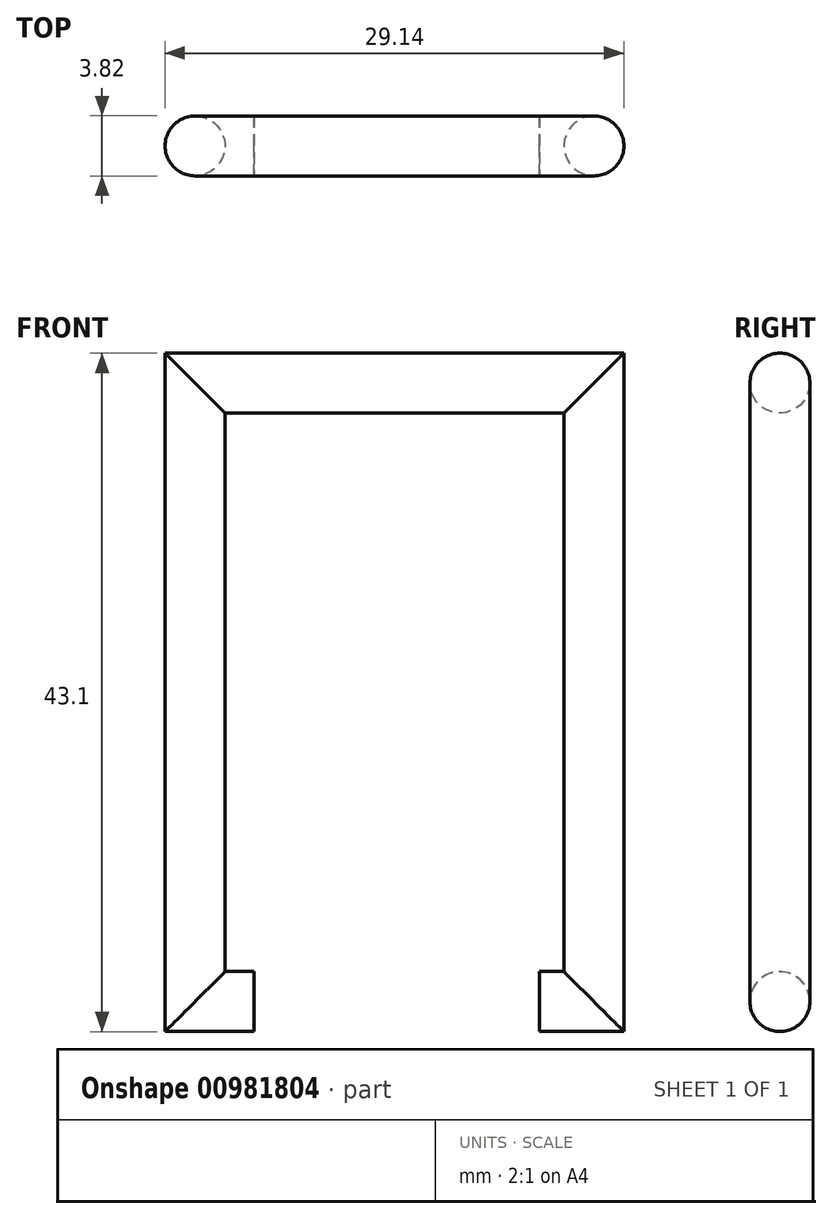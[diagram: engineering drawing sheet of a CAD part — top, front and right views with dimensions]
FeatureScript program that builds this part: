
annotation { "Feature Type Name" : "Feature", "Feature Type Description" : "" }
export const myFeature = defineFeature(function(context is Context, id is Id, definition is map)
    precondition{}
    {
        {
            var Q0;
            Q0=qCreatedBy(makeId("Front.planeOp"),FACE);
            var sketch = newSketch(context, id + "F0", { "sketchPlane" : qUnion([Q0])});
            skLineSegment(sketch, "E0", {"start": v(-9.93, 0) * mm, "end": v(-13.67, 0) * mm});
            skLineSegment(sketch, "E1", {"start": v(-13.67, 0) * mm, "end": v(-13.67, 39.29) * mm});
            skLineSegment(sketch, "E2", {"start": v(-13.67, 39.29) * mm, "end": v(11.66, 39.29) * mm});
            skLineSegment(sketch, "E3", {"start": v(11.66, 39.29) * mm, "end": v(11.66, 0) * mm});
            skLineSegment(sketch, "E4", {"start": v(11.66, 0) * mm, "end": v(8.2, 0) * mm});
            skSolve(sketch);
        }
        {
            var Q0;
            Q0=qCreatedBy(makeId("Right.planeOp"),FACE);
            cPlane(context, id + "F1", {"entities" : qUnion([Q0]), "cplaneType" : CPlaneType.OFFSET, "offset" : 10.03 * mm, "oppositeDirection" : true, "width" : 152.4 * mm, "height" : 152.4 * mm});
        }
        {
            var Q0;
            Q0=qCreatedBy(id+"F1.planeOp",FACE);
            var sketch = newSketch(context, id + "F2", { "sketchPlane" : qUnion([Q0])});
            skCircle(sketch, "E5", {"center": v(0, 0) * mm, "radius": 1.9 * mm});
            skSolve(sketch);
        }
        {
            var Q0;
            Q0=makeQuery(id+"F2.imprint","IMPRINT",FACE,{"disambiguationData":[TD([[makeQuery(id+"F2.imprint","IMPRINT",EDGE,{"derivedFrom":sQuery(id+"F2.wireOp",EDGE,"E5")}),1.0]])]});
            var Q1;
            Q1=sQuery(id+"F0.wireOp",EDGE,"E0");
            var Q2;
            Q2=sQuery(id+"F0.wireOp",EDGE,"E1");
            var Q3;
            Q3=sQuery(id+"F0.wireOp",EDGE,"E2");
            var Q4;
            Q4=sQuery(id+"F0.wireOp",EDGE,"E3");
            var Q5;
            Q5=sQuery(id+"F0.wireOp",EDGE,"E4");
            sweep(context, id + "F3", {"profiles" : qUnion([Q0]), "path" : qUnion([Q1, Q2, Q3, Q4, Q5])});
        }
    });
